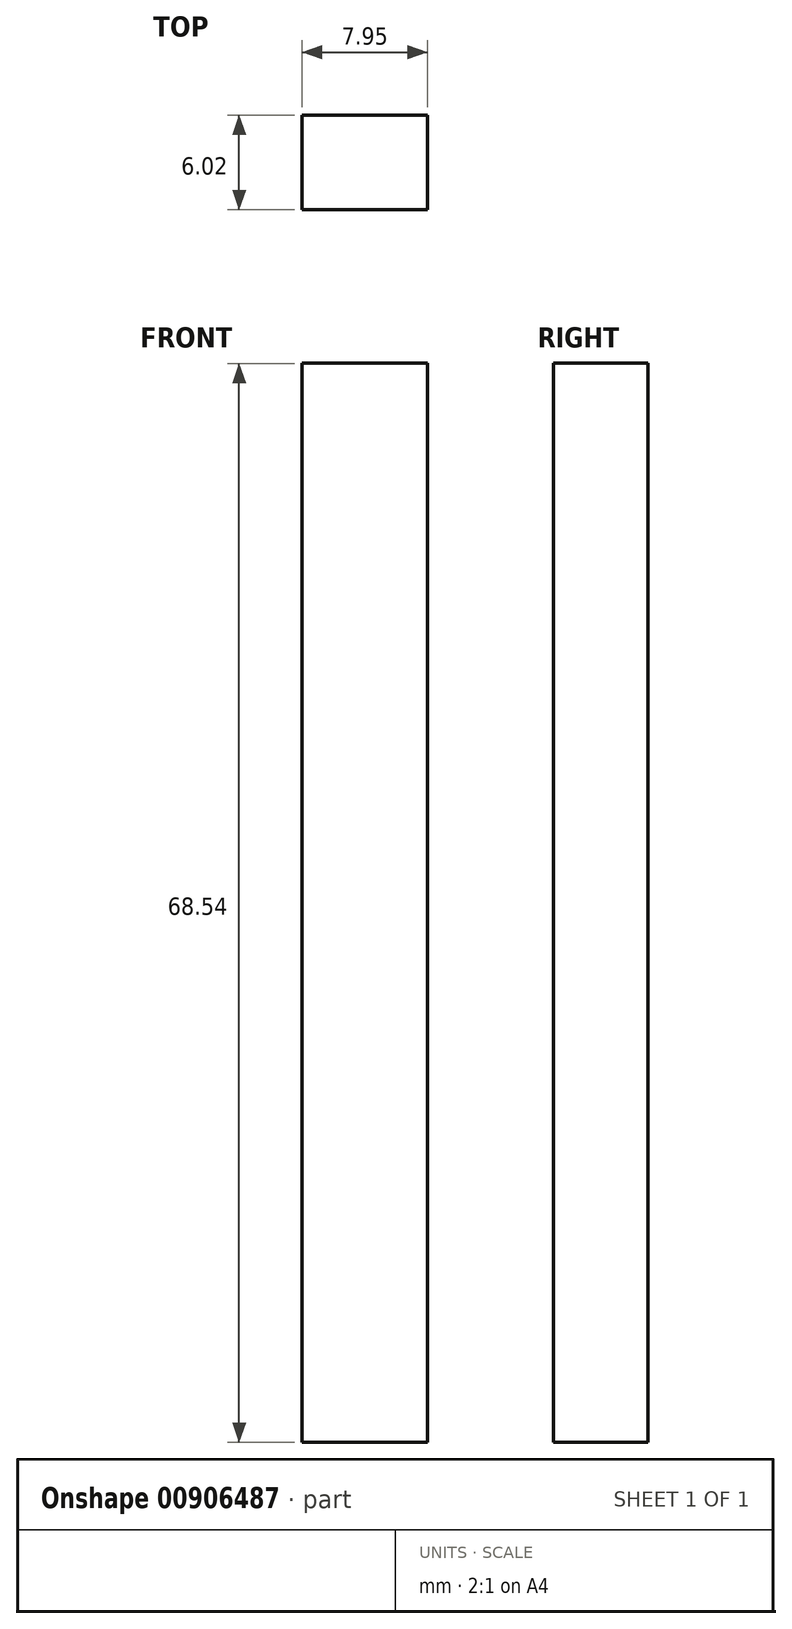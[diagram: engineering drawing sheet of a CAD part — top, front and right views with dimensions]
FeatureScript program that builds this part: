
annotation { "Feature Type Name" : "Feature", "Feature Type Description" : "" }
export const myFeature = defineFeature(function(context is Context, id is Id, definition is map)
    precondition{}
    {
        {
            var Q0;
            Q0=qCreatedBy(makeId("Front.planeOp"),FACE);
            var sketch = newSketch(context, id + "F0", { "sketchPlane" : qUnion([Q0])});
            skLineSegment(sketch, "E0.bottom", {"start": v(-51.27, 47.74) * mm, "end": v(-43.32, 47.74) * mm});
            skLineSegment(sketch, "E0.top", {"start": v(-51.27, -20.8) * mm, "end": v(-43.32, -20.8) * mm});
            skLineSegment(sketch, "E0.left", {"start": v(-51.27, 47.74) * mm, "end": v(-51.27, -20.8) * mm});
            skLineSegment(sketch, "E0.right", {"start": v(-43.32, 47.74) * mm, "end": v(-43.32, -20.8) * mm});
            skSolve(sketch);
        }
        {
            var Q0;
            Q0 = qSketchRegion(id + "F0", true);
            extrude(context, id + "F1", {"entities" : qUnion([Q0]), "depth" : 6.02 * mm, "offsetDistance" : 25.4 * mm});
        }
    });
